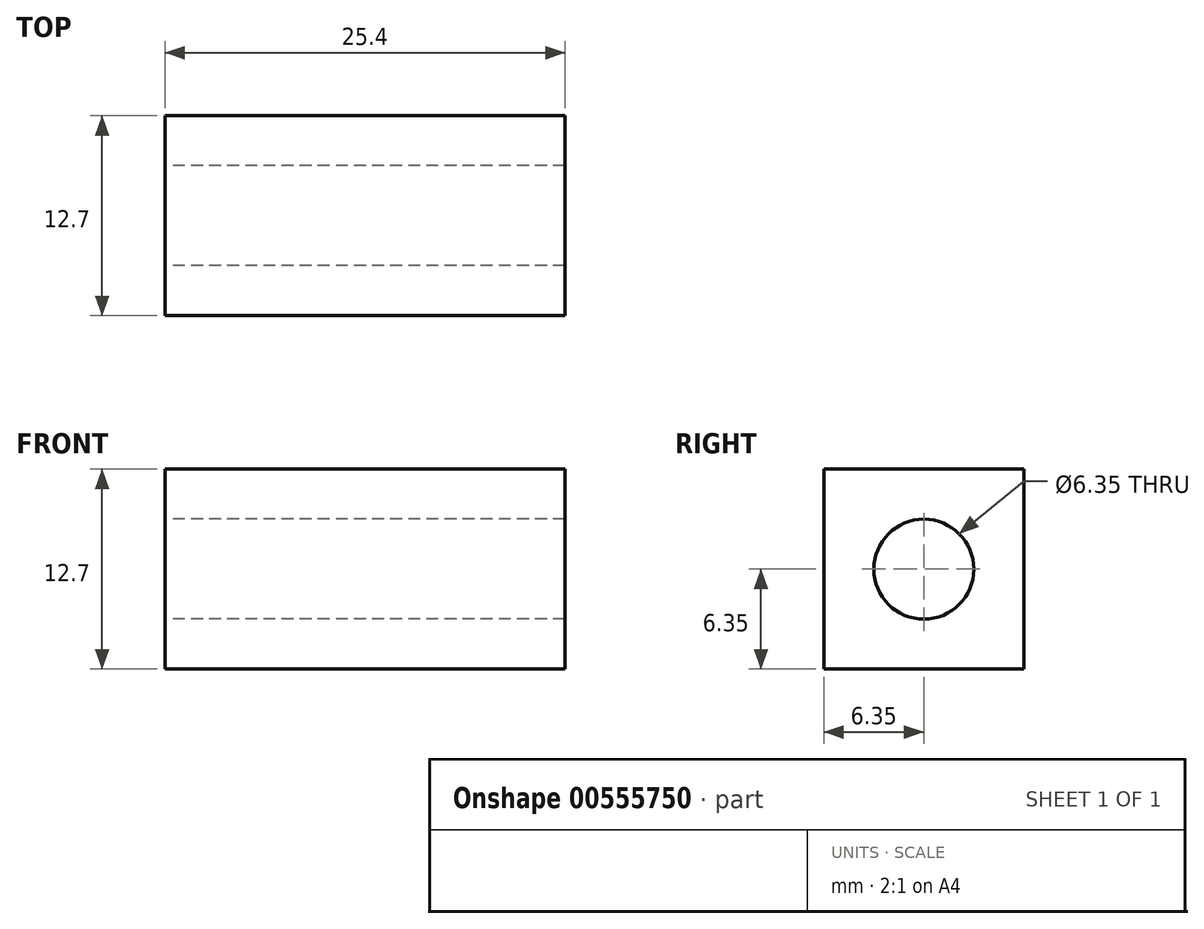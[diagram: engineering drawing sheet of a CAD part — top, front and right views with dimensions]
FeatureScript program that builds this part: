
annotation { "Feature Type Name" : "Feature", "Feature Type Description" : "" }
export const myFeature = defineFeature(function(context is Context, id is Id, definition is map)
    precondition{}
    {
        {
            var Q0;
            Q0=qCreatedBy(makeId("Right.planeOp"),FACE);
            var sketch = newSketch(context, id + "F0", { "sketchPlane" : qUnion([Q0])});
            skLineSegment(sketch, "E0.bottom", {"start": v(0, 0) * mm, "end": v(12.7, 0) * mm});
            skLineSegment(sketch, "E0.top", {"start": v(0, 12.7) * mm, "end": v(12.7, 12.7) * mm});
            skLineSegment(sketch, "E0.left", {"start": v(0, 0) * mm, "end": v(0, 12.7) * mm});
            skLineSegment(sketch, "E0.right", {"start": v(12.7, 0) * mm, "end": v(12.7, 12.7) * mm});
            skCircle(sketch, "E1", {"center": v(6.35, 6.35) * mm, "radius": 3.18 * mm});
            skPoint(sketch, "E1.centerSnap0", {"position": v(6.35, 0) * mm});
            skSolve(sketch);
        }
        {
            var Q0;
            Q0=makeQuery(id+"F0.imprint","IMPRINT",FACE,{"disambiguationData":[TD([[makeQuery(id+"F0.imprint","IMPRINT",EDGE,{"derivedFrom":sQuery(id+"F0.wireOp",EDGE,"E0.bottom")}),1.0]])]});
            extrude(context, id + "F1", {"entities" : qUnion([Q0]), "depth" : 25.4 * mm, "offsetDistance" : 25.4 * mm});
        }
    });
